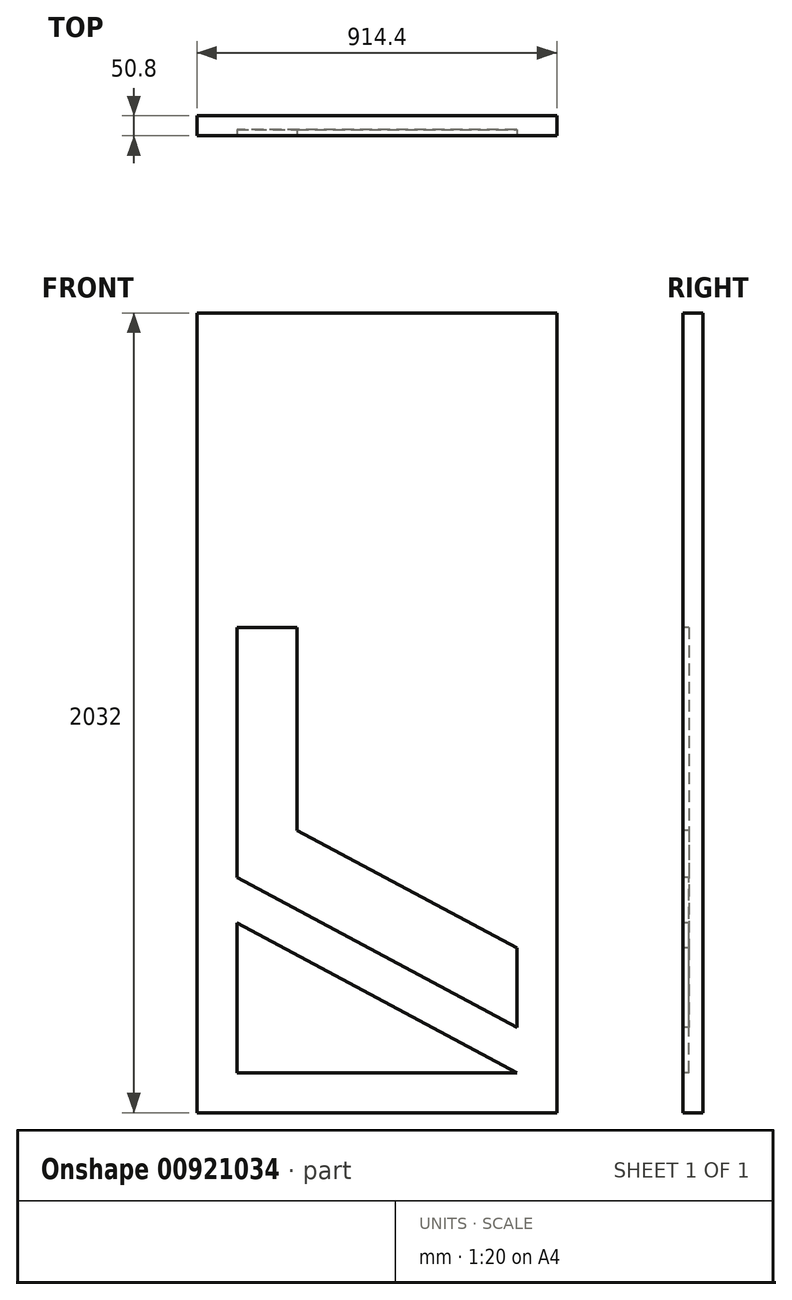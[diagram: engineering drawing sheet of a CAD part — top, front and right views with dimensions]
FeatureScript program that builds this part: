
annotation { "Feature Type Name" : "Feature", "Feature Type Description" : "" }
export const myFeature = defineFeature(function(context is Context, id is Id, definition is map)
    precondition{}
    {
        {
            var Q0;
            Q0=qCreatedBy(makeId("Front.planeOp"),FACE);
            var sketch = newSketch(context, id + "F0", { "sketchPlane" : qUnion([Q0])});
            skLineSegment(sketch, "E0.bottom", {"start": v(0, 0) * mm, "end": v(914.4, 0) * mm});
            skLineSegment(sketch, "E0.top", {"start": v(0, 2032) * mm, "end": v(914.4, 2032) * mm});
            skLineSegment(sketch, "E0.left", {"start": v(0, 0) * mm, "end": v(0, 2032) * mm});
            skLineSegment(sketch, "E0.right", {"start": v(914.4, 0) * mm, "end": v(914.4, 2032) * mm});
            skSolve(sketch);
        }
        {
            var Q0;
            Q0 = qSketchRegion(id + "F0", true);
            extrude(context, id + "F1", {"entities" : qUnion([Q0]), "depth" : 50.8 * mm, "offsetDistance" : 25.4 * mm});
        }
        {
            var Q0;
            Q0=makeQuery(id+"F1.opExtrude","CAP_FACE",FACE,{"disambiguationData":[OSD([sQuery(id+"F0.wireOp",EDGE,"E0.bottom"),sQuery(id+"F0.wireOp",EDGE,"E0.top"),sQuery(id+"F0.wireOp",EDGE,"E0.left"),sQuery(id+"F0.wireOp",EDGE,"E0.right")])],"isStart":false});
            var sketch = newSketch(context, id + "F2", { "sketchPlane" : qUnion([Q0])});
            skLineSegment(sketch, "E1", {"start": v(101.6, 1930.4) * mm, "end": v(101.6, 1549.4) * mm});
            skLineSegment(sketch, "E2", {"start": v(101.6, 1549.4) * mm, "end": v(101.6, 1930.4) * mm});
            skLineSegment(sketch, "E3", {"start": v(812.8, 1930.4) * mm, "end": v(101.6, 1930.4) * mm});
            skLineSegment(sketch, "E4", {"start": v(812.8, 1930.4) * mm, "end": v(101.6, 1549.4) * mm});
            skLineSegment(sketch, "E5", {"start": v(101.6, 1434.14) * mm, "end": v(101.6, 799.14) * mm});
            skLineSegment(sketch, "E6", {"start": v(812.8, 1613.86) * mm, "end": v(812.8, 1815.14) * mm});
            skLineSegment(sketch, "E7", {"start": v(812.8, 1815.14) * mm, "end": v(101.6, 1434.14) * mm});
            skLineSegment(sketch, "E8", {"start": v(-617.88, 1016) * mm, "end": v(1442.75, 1016) * mm, "construction": true});
            skLineSegment(sketch, "E9.MirrorCS", {"start": v(101.6, 597.86) * mm, "end": v(101.6, 1232.86) * mm});
            skLineSegment(sketch, "E10.MirrorCS", {"start": v(812.8, 418.14) * mm, "end": v(812.8, 216.86) * mm});
            skLineSegment(sketch, "E11.MirrorCS", {"start": v(812.8, 216.86) * mm, "end": v(101.6, 597.86) * mm});
            skLineSegment(sketch, "E12.MirrorCS", {"start": v(812.8, 101.6) * mm, "end": v(101.6, 482.6) * mm});
            skLineSegment(sketch, "E13.MirrorCS", {"start": v(101.6, 101.6) * mm, "end": v(101.6, 482.6) * mm});
            skLineSegment(sketch, "E14.MirrorCS", {"start": v(812.8, 101.6) * mm, "end": v(101.6, 101.6) * mm});
            skPoint(sketch, "E15", {"position": v(506.4, 1016) * mm});
            skPoint(sketch, "E16.orphan", {"position": v(101.6, 1232.86) * mm});
            skLineSegment(sketch, "E17", {"start": v(254, 1314.5) * mm, "end": v(812.8, 1613.86) * mm});
            skLineSegment(sketch, "E18", {"start": v(254, 717.5) * mm, "end": v(812.8, 418.14) * mm});
            skLineSegment(sketch, "E19", {"start": v(254, 1314.5) * mm, "end": v(254, 717.5) * mm});
            skPoint(sketch, "E20.end.orphan", {"position": v(812.8, 1180.14) * mm});
            skPoint(sketch, "E21.MirrorCS.end.orphan", {"position": v(812.8, 851.86) * mm});
            skLineSegment(sketch, "E22", {"start": v(101.6, 1232.86) * mm, "end": v(254, 1232.86) * mm});
            skLineSegment(sketch, "E23", {"start": v(101.6, 799.14) * mm, "end": v(254, 799.14) * mm});
            skSolve(sketch);
        }
        {
            var Q0;
            Q0=makeQuery(id+"F2.imprint","IMPRINT",FACE,{"disambiguationData":[TD([[makeQuery(id+"F2.imprint","IMPRINT",EDGE,{"derivedFrom":sQuery(id+"F2.wireOp",EDGE,"E5")}),1.0]])]});
            var Q1;
            {var subQ0=sQuery(id+"F2.wireOp",EDGE,"E22");Q1=makeQuery(id+"F2.imprint","IMPRINT",FACE,{"disambiguationData":[TD([[makeQuery(id+"F2.imprint","IMPRINT",EDGE,{"derivedFrom":subQ0}),-1.0]])]});}
            var Q2;
            Q2=makeQuery(id+"F2.imprint","IMPRINT",FACE,{"disambiguationData":[TD([[makeQuery(id+"F2.imprint","IMPRINT",EDGE,{"derivedFrom":sQuery(id+"F2.wireOp",EDGE,"E2")}),-1.0]])]});
            var Q3;
            Q3=makeQuery(id+"F2.imprint","IMPRINT",FACE,{"disambiguationData":[TD([[makeQuery(id+"F2.imprint","IMPRINT",EDGE,{"derivedFrom":sQuery(id+"F2.wireOp",EDGE,"E10.MirrorCS")}),-1.0]])]});
            var Q4;
            Q4=makeQuery(id+"F2.imprint","IMPRINT",FACE,{"disambiguationData":[TD([[makeQuery(id+"F2.imprint","IMPRINT",EDGE,{"derivedFrom":sQuery(id+"F2.wireOp",EDGE,"E12.MirrorCS")}),1.0]])]});
            extrude(context, id + "F3", {"entities" : qUnion([Q0, Q1, Q2, Q3, Q4]), "operationType" : NewBodyOperationType.REMOVE, "oppositeDirection" : true, "depth" : 15.24 * mm, "offsetDistance" : 25.4 * mm});
        }
    });
